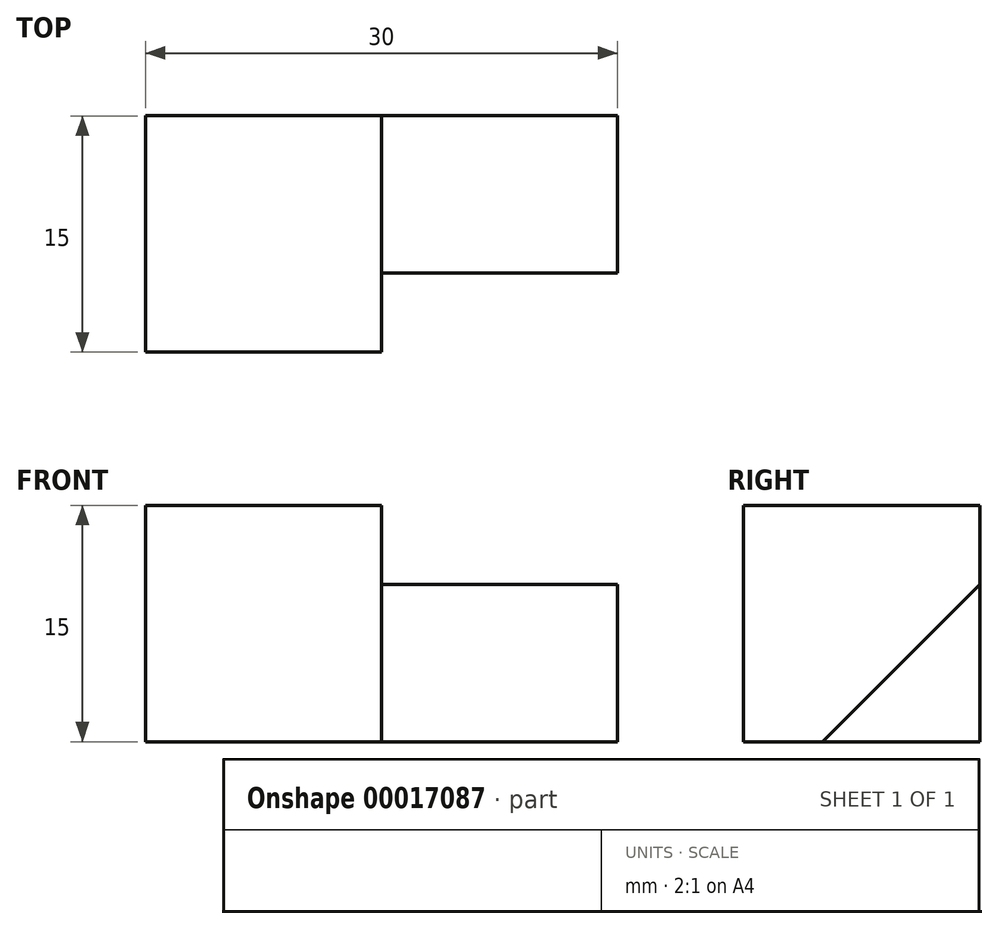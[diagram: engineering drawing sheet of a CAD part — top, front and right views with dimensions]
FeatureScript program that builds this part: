
annotation { "Feature Type Name" : "Feature", "Feature Type Description" : "" }
export const myFeature = defineFeature(function(context is Context, id is Id, definition is map)
    precondition{}
    {
        {
            var Q0;
            Q0=qCreatedBy(makeId("Right.planeOp"),FACE);
            var sketch = newSketch(context, id + "F0", { "sketchPlane" : qUnion([Q0])});
            skLineSegment(sketch, "E0.bottom", {"start": v(-43.29, 39.38) * mm, "end": v(-28.29, 39.38) * mm});
            skLineSegment(sketch, "E0.top", {"start": v(-43.29, 24.38) * mm, "end": v(-28.29, 24.38) * mm});
            skLineSegment(sketch, "E0.left", {"start": v(-43.29, 39.38) * mm, "end": v(-43.29, 24.38) * mm});
            skLineSegment(sketch, "E0.right", {"start": v(-28.29, 39.38) * mm, "end": v(-28.29, 24.38) * mm});
            skSolve(sketch);
        }
        {
            var Q0;
            Q0=makeQuery(id+"F0.imprint","IMPRINT",FACE,{"disambiguationData":[TD([[makeQuery(id+"F0.imprint","IMPRINT",EDGE,{"derivedFrom":sQuery(id+"F0.wireOp",EDGE,"E0.bottom")}),-1.0]])]});
            extrude(context, id + "F1", {"entities" : qUnion([Q0]), "depth" : 15 * mm});
        }
        {
            var Q0;
            Q0=makeQuery(id+"F1.opExtrude","CAP_FACE",FACE,{"disambiguationData":[OSD([sQuery(id+"F0.wireOp",EDGE,"E0.bottom"),sQuery(id+"F0.wireOp",EDGE,"E0.top"),sQuery(id+"F0.wireOp",EDGE,"E0.left"),sQuery(id+"F0.wireOp",EDGE,"E0.right")])],"isStart":false});
            var sketch = newSketch(context, id + "F2", { "sketchPlane" : qUnion([Q0])});
            skLineSegment(sketch, "E1", {"start": v(-28.29, 34.38) * mm, "end": v(-38.29, 24.38) * mm});
            skLineSegment(sketch, "E2", {"start": v(-38.29, 24.38) * mm, "end": v(-28.29, 24.38) * mm});
            skLineSegment(sketch, "E3", {"start": v(-28.29, 24.38) * mm, "end": v(-28.29, 34.38) * mm});
            skSolve(sketch);
        }
        {
            var Q0;
            Q0=makeQuery(id+"F2.imprint","IMPRINT",FACE,{"disambiguationData":[TD([[makeQuery(id+"F2.imprint","IMPRINT",EDGE,{"derivedFrom":sQuery(id+"F2.wireOp",EDGE,"E1")}),1.0]])]});
            extrude(context, id + "F3", {"entities" : qUnion([Q0]), "operationType" : NewBodyOperationType.ADD, "depth" : 15 * mm});
        }
    });
